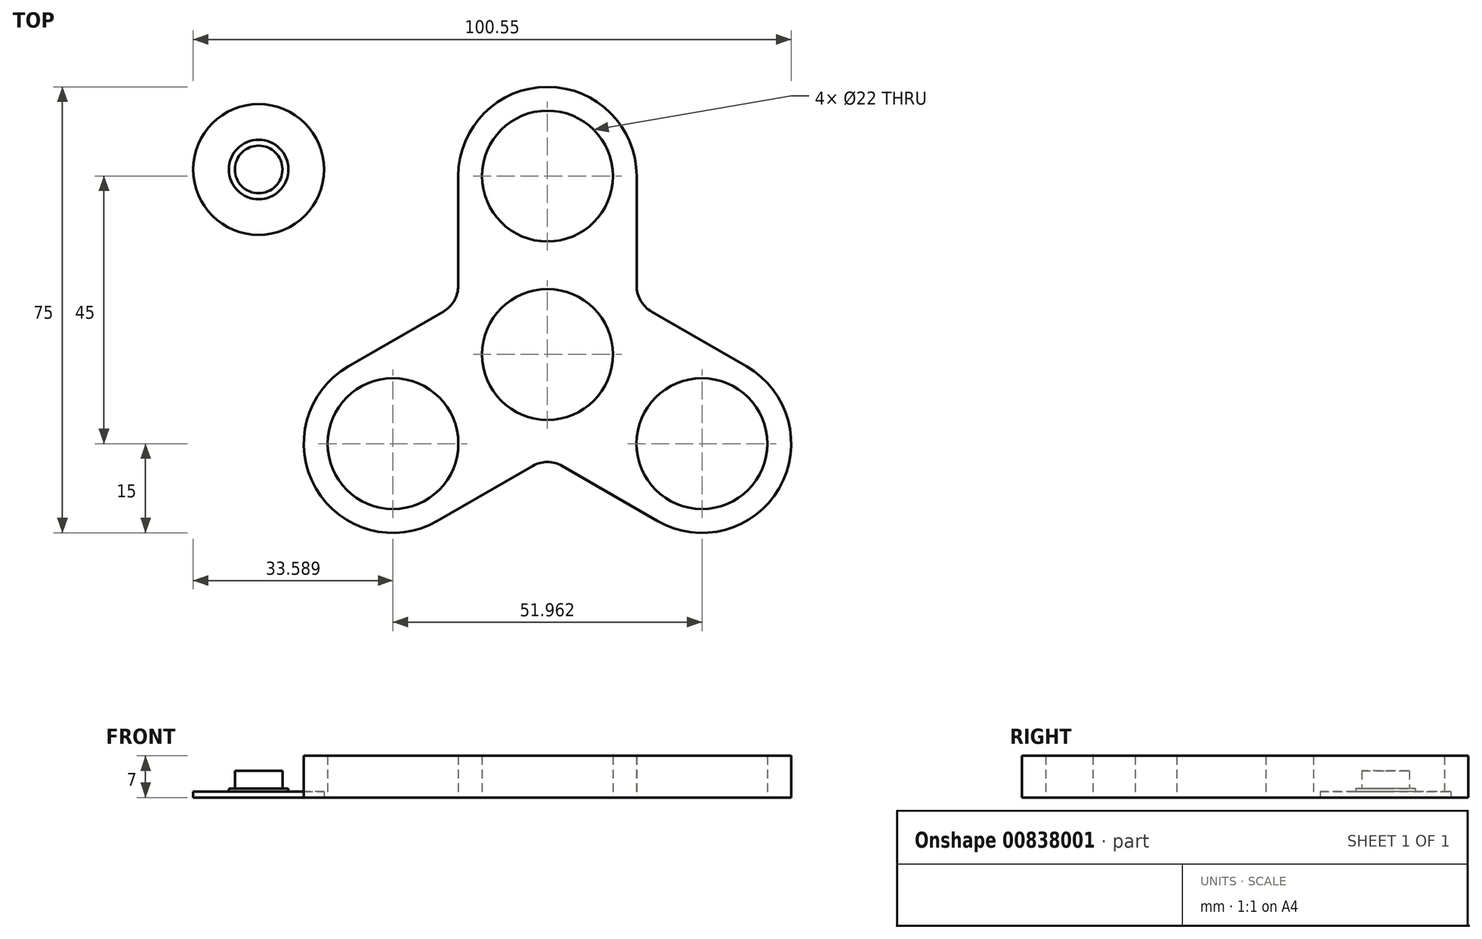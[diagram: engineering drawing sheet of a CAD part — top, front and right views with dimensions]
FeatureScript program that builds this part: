
annotation { "Feature Type Name" : "Feature", "Feature Type Description" : "" }
export const myFeature = defineFeature(function(context is Context, id is Id, definition is map)
    precondition{}
    {
        {
            var Q0;
            Q0=qCreatedBy(makeId("Top.planeOp"),FACE);
            var sketch = newSketch(context, id + "F0", { "sketchPlane" : qUnion([Q0])});
            skCircle(sketch, "E0", {"center": v(0, 0) * mm, "radius": 15 * mm});
            skArc(sketch, "E1", {"start": v(15, 30) * mm, "mid": v(0, 45) * mm, "end": v(-15, 30) * mm});
            skCircle(sketch, "E2", {"center": v(0, 0) * mm, "radius": 11 * mm});
            skLineSegment(sketch, "E3", {"start": v(0, 51.93) * mm, "end": v(0, 0) * mm, "construction": true});
            skLineSegment(sketch, "E4", {"start": v(-15, 30) * mm, "end": v(-15, 11.55) * mm});
            skLineSegment(sketch, "E5", {"start": v(15, 30) * mm, "end": v(15, 11.55) * mm});
            skArc(sketch, "E6.1.0", {"start": v(-33.48, -2) * mm, "mid": v(-38.97, -22.5) * mm, "end": v(-18.48, -28) * mm});
            skLineSegment(sketch, "E6.1.1", {"start": v(-33.48, -2) * mm, "end": v(-17.5, 7.22) * mm});
            skLineSegment(sketch, "E6.1.2", {"start": v(-18.48, -28) * mm, "end": v(-2.5, -18.76) * mm});
            skArc(sketch, "E6.2.0", {"start": v(18.48, -28) * mm, "mid": v(38.97, -22.5) * mm, "end": v(33.48, -2) * mm});
            skLineSegment(sketch, "E6.2.1", {"start": v(18.48, -28) * mm, "end": v(2.5, -18.76) * mm});
            skLineSegment(sketch, "E6.2.2", {"start": v(33.48, -2) * mm, "end": v(17.5, 7.22) * mm});
            skPoint(sketch, "E7.orphan", {"position": v(-7.5, 13) * mm});
            skPoint(sketch, "E8.orphan", {"position": v(-15, 0) * mm});
            skPoint(sketch, "E9.orphan", {"position": v(-7.5, -13) * mm});
            skPoint(sketch, "E10.orphan", {"position": v(7.5, -13) * mm});
            skPoint(sketch, "E11.orphan", {"position": v(15, 0) * mm});
            skPoint(sketch, "E12.orphan", {"position": v(7.5, 13) * mm});
            skPoint(sketch, "E13.visualSharp", {"position": v(15, 8.66) * mm});
            skArc(sketch, "E13.filletArc", {"start": v(15, 11.55) * mm, "mid": v(15.67, 9.05) * mm, "end": v(17.5, 7.22) * mm});
            skPoint(sketch, "E14.visualSharp", {"position": v(0, -17.32) * mm});
            skArc(sketch, "E14.filletArc", {"start": v(2.5, -18.76) * mm, "mid": v(0, -18.1) * mm, "end": v(-2.5, -18.76) * mm});
            skPoint(sketch, "E15.visualSharp", {"position": v(-15, 8.66) * mm});
            skArc(sketch, "E15.filletArc", {"start": v(-17.5, 7.22) * mm, "mid": v(-15.67, 9.05) * mm, "end": v(-15, 11.55) * mm});
            skCircle(sketch, "E16", {"center": v(0, 30) * mm, "radius": 11 * mm});
            skCircle(sketch, "E17", {"center": v(-25.98, -15) * mm, "radius": 11 * mm});
            skCircle(sketch, "E18", {"center": v(25.98, -15) * mm, "radius": 11 * mm});
            skCircle(sketch, "E19", {"center": v(-48.57, 31.1) * mm, "radius": 11 * mm});
            skCircle(sketch, "E20", {"center": v(-48.57, 31.1) * mm, "radius": 5 * mm});
            skCircle(sketch, "E21", {"center": v(-48.57, 31.1) * mm, "radius": 4 * mm});
            skSolve(sketch);
        }
        {
            var Q0;
            Q0=makeQuery(id+"F0.imprint","IMPRINT",FACE,{"disambiguationData":[TD([[makeQuery(id+"F0.imprint","IMPRINT",EDGE,{"derivedFrom":sQuery(id+"F0.wireOp",EDGE,"E0")}),-1.0]])]});
            var Q1;
            Q1=makeQuery(id+"F0.imprint","IMPRINT",FACE,{"disambiguationData":[TD([[makeQuery(id+"F0.imprint","IMPRINT",EDGE,{"derivedFrom":sQuery(id+"F0.wireOp",EDGE,"E0")}),1.0]])]});
            extrude(context, id + "F1", {"entities" : qUnion([Q0, Q1]), "depth" : 7 * mm, "offsetDistance" : 25 * mm});
        }
        {
            var Q0;
            Q0=makeQuery(id+"F0.imprint","IMPRINT",FACE,{"disambiguationData":[TD([[makeQuery(id+"F0.imprint","IMPRINT",EDGE,{"derivedFrom":sQuery(id+"F0.wireOp",EDGE,"E21")}),1.0]])]});
            extrude(context, id + "F2", {"entities" : qUnion([Q0]), "depth" : 4.5 * mm, "offsetDistance" : 25 * mm});
        }
        {
            var Q0;
            Q0=makeQuery(id+"F0.imprint","IMPRINT",FACE,{"disambiguationData":[TD([[makeQuery(id+"F0.imprint","IMPRINT",EDGE,{"derivedFrom":sQuery(id+"F0.wireOp",EDGE,"E20")}),1.0]])]});
            extrude(context, id + "F3", {"entities" : qUnion([Q0]), "operationType" : NewBodyOperationType.ADD, "depth" : 1.5 * mm, "offsetDistance" : 25 * mm});
        }
        {
            var Q0;
            Q0=makeQuery(id+"F0.imprint","IMPRINT",FACE,{"disambiguationData":[TD([[makeQuery(id+"F0.imprint","IMPRINT",EDGE,{"derivedFrom":sQuery(id+"F0.wireOp",EDGE,"E19")}),1.0]])]});
            extrude(context, id + "F4", {"entities" : qUnion([Q0]), "operationType" : NewBodyOperationType.ADD, "depth" : 1 * mm, "offsetDistance" : 25 * mm});
        }
    });
